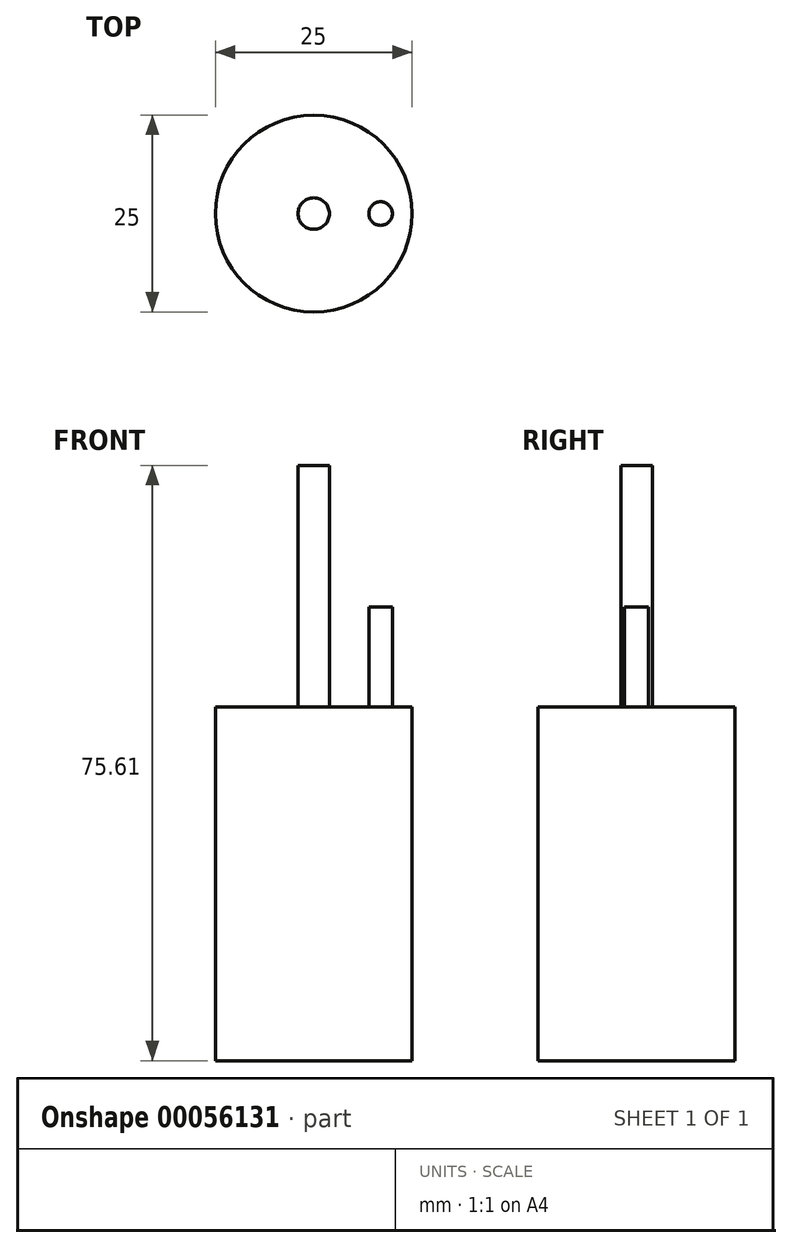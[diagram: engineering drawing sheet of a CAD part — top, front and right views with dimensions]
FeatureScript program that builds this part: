
annotation { "Feature Type Name" : "Feature", "Feature Type Description" : "" }
export const myFeature = defineFeature(function(context is Context, id is Id, definition is map)
    precondition{}
    {
        {
            var Q0;
            Q0=qCreatedBy(makeId("Top.planeOp"),FACE);
            var sketch = newSketch(context, id + "F0", { "sketchPlane" : qUnion([Q0])});
            skCircle(sketch, "E0", {"center": v(0, 0) * mm, "radius": 12.5 * mm});
            skSolve(sketch);
        }
        {
            var Q0;
            Q0=makeQuery(id+"F0.imprint","IMPRINT",FACE,{"disambiguationData":[TD([[makeQuery(id+"F0.imprint","IMPRINT",EDGE,{"derivedFrom":sQuery(id+"F0.wireOp",EDGE,"E0")}),1.0]])]});
            extrude(context, id + "F1", {"entities" : qUnion([Q0]), "depth" : 57.6 * mm});
        }
        {
            var Q0;
            Q0=makeQuery(id+"F1.opExtrude","CAP_FACE",FACE,{"disambiguationData":[OSD([sQuery(id+"F0.wireOp",EDGE,"E0")])],"isStart":false});
            var sketch = newSketch(context, id + "F2", { "sketchPlane" : qUnion([Q0])});
            skCircle(sketch, "E1", {"center": v(0, 0) * mm, "radius": 2 * mm});
            skSolve(sketch);
        }
        {
            var Q0;
            Q0=makeQuery(id+"F2.imprint","IMPRINT",FACE,{"disambiguationData":[TD([[makeQuery(id+"F2.imprint","IMPRINT",EDGE,{"derivedFrom":sQuery(id+"F2.wireOp",EDGE,"E1")}),1.0]])]});
            extrude(context, id + "F3", {"entities" : qUnion([Q0]), "operationType" : NewBodyOperationType.ADD, "depth" : 18 * mm});
        }
        {
            var Q0;
            Q0=makeQuery(id+"F1.opExtrude","CAP_FACE",FACE,{"disambiguationData":[OSD([sQuery(id+"F0.wireOp",EDGE,"E0")])],"isStart":false});
            var sketch = newSketch(context, id + "F4", { "sketchPlane" : qUnion([Q0])});
            skCircle(sketch, "E2", {"center": v(-8.5, 0) * mm, "radius": 1.5 * mm});
            skCircle(sketch, "E3.0", {"center": v(0, 0) * mm, "radius": 2 * mm, "construction": true});
            skLineSegment(sketch, "E4", {"start": v(0, 0) * mm, "end": v(0, -12.5) * mm, "construction": true});
            skCircle(sketch, "E5.MirrorC", {"center": v(8.5, 0) * mm, "radius": 1.5 * mm});
            skSolve(sketch);
        }
        {
            var Q0;
            Q0=makeQuery(id+"F4.imprint","IMPRINT",FACE,{"disambiguationData":[TD([[makeQuery(id+"F4.imprint","IMPRINT",EDGE,{"derivedFrom":sQuery(id+"F4.wireOp",EDGE,"E2")}),1.0]])]});
            var Q1;
            Q1=makeQuery(id+"F4.imprint","IMPRINT",FACE,{"disambiguationData":[TD([[makeQuery(id+"F4.imprint","IMPRINT",EDGE,{"derivedFrom":sQuery(id+"F4.wireOp",EDGE,"E5.MirrorC")}),-1.0]])]});
            extrude(context, id + "F5", {"entities" : qUnion([Q0, Q1]), "operationType" : NewBodyOperationType.REMOVE, "oppositeDirection" : true, "depth" : 12.7 * mm});
        }
    });
